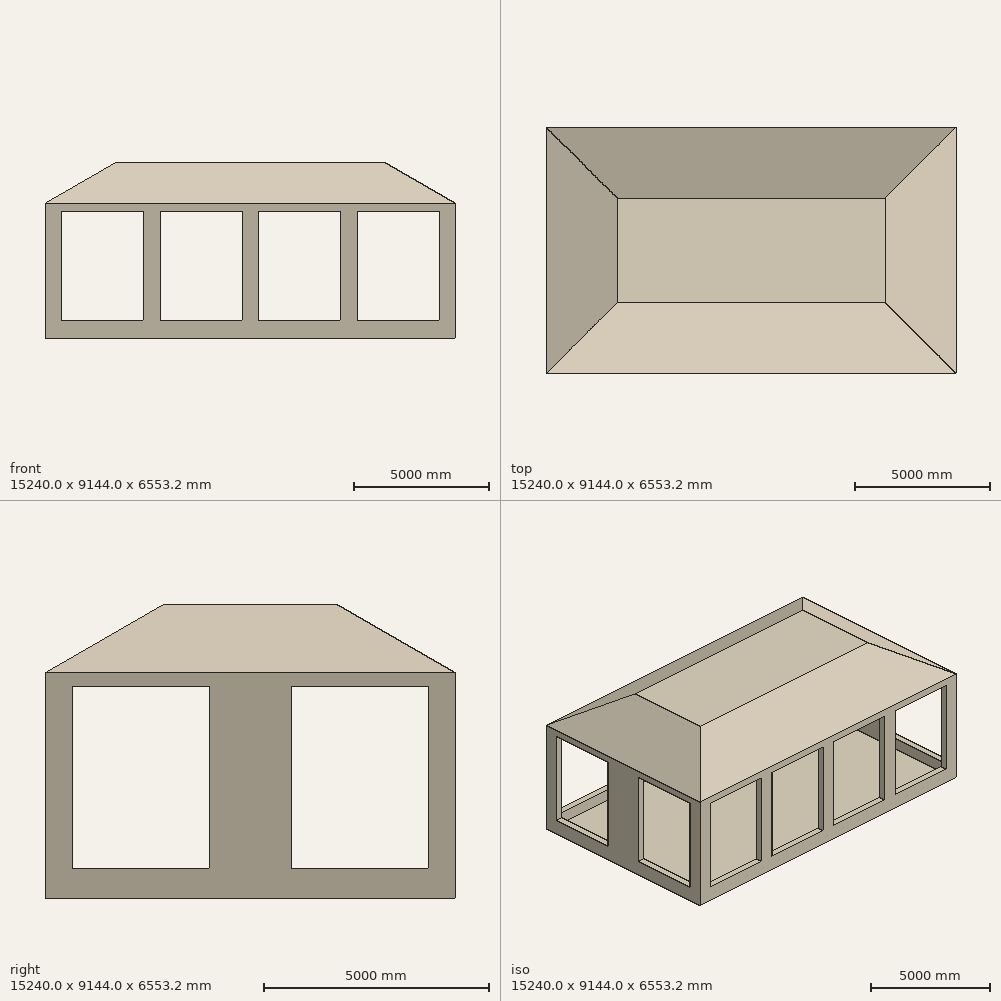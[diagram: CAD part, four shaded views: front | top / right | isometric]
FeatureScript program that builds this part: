
annotation { "Feature Type Name" : "Feature", "Feature Type Description" : "" }
export const myFeature = defineFeature(function(context is Context, id is Id, definition is map)
    precondition{}
    {
        {
            var Q0;
            Q0=qCreatedBy(makeId("Front.planeOp"),FACE);
            var sketch = newSketch(context, id + "F0", { "sketchPlane" : qUnion([Q0])});
            skLineSegment(sketch, "E0.bottom", {"start": v(-2747.34, 3105.4) * mm, "end": v(12492.66, 3105.4) * mm});
            skLineSegment(sketch, "E0.top", {"start": v(-2747.34, -1771.4) * mm, "end": v(12492.66, -1771.4) * mm});
            skLineSegment(sketch, "E0.left", {"start": v(-2747.34, 3105.4) * mm, "end": v(-2747.34, -1771.4) * mm});
            skLineSegment(sketch, "E0.right", {"start": v(12492.66, 3105.4) * mm, "end": v(12492.66, -1771.4) * mm});
            skSolve(sketch);
        }
        {
            var Q0;
            Q0 = qSketchRegion(id + "F0", true);
            extrude(context, id + "F1", {"entities" : qUnion([Q0]), "depth" : 9144 * mm});
        }
        {
            var Q0;
            Q0=makeQuery(id+"F1.opExtrude","SWEPT_FACE",FACE,{"disambiguationData":[OSD([sQuery(id+"F0.wireOp",EDGE,"E0.bottom")])]});
            var sketch = newSketch(context, id + "F2", { "sketchPlane" : qUnion([Q0])});
            skLineSegment(sketch, "E1.bottom", {"start": v(-2747.34, 0) * mm, "end": v(12492.66, 0) * mm});
            skLineSegment(sketch, "E1.top", {"start": v(-2747.34, -9144) * mm, "end": v(12492.66, -9144) * mm});
            skLineSegment(sketch, "E1.left", {"start": v(-2747.34, 0) * mm, "end": v(-2747.34, -9144) * mm});
            skLineSegment(sketch, "E1.right", {"start": v(12492.66, 0) * mm, "end": v(12492.66, -9144) * mm});
            skSolve(sketch);
        }
        {
            var Q0;
            Q0 = qSketchRegion(id + "F2", true);
            extrude(context, id + "F3", {"entities" : qUnion([Q0]), "operationType" : NewBodyOperationType.ADD, "depth" : 1524 * mm, "hasDraft" : true, "draftAngle" : 60 * degree, "draftPullDirection" : true});
        }
        {
            var Q0;
            Q0=makeQuery(id+"F1.opExtrude","SWEPT_FACE",FACE,{"disambiguationData":[OSD([sQuery(id+"F0.wireOp",EDGE,"E0.top")])]});
            shell(context, id + "F4", {"entities" : qUnion([Q0]), "thickness" : 304.8 * mm});
        }
        {
            var Q0;
            Q0=makeQuery(id+"F1.opExtrude","CAP_FACE",FACE,{"disambiguationData":[OSD([sQuery(id+"F0.wireOp",EDGE,"E0.bottom"),sQuery(id+"F0.wireOp",EDGE,"E0.top"),sQuery(id+"F0.wireOp",EDGE,"E0.left"),sQuery(id+"F0.wireOp",EDGE,"E0.right")])],"isStart":false});
            var sketch = newSketch(context, id + "F5", { "sketchPlane" : qUnion([Q0])});
            skLineSegment(sketch, "E2.bottom", {"start": v(-2137.74, 2800.6) * mm, "end": v(910.26, 2800.6) * mm});
            skLineSegment(sketch, "E2.top", {"start": v(-2137.74, -1263.4) * mm, "end": v(910.26, -1263.4) * mm});
            skLineSegment(sketch, "E2.left", {"start": v(-2137.74, 2800.6) * mm, "end": v(-2137.74, -1263.4) * mm});
            skLineSegment(sketch, "E2.right", {"start": v(910.26, 2800.6) * mm, "end": v(910.26, -1263.4) * mm});
            skLineSegment(sketch, "E3.bottom", {"start": v(1519.86, 2800.6) * mm, "end": v(4567.86, 2800.6) * mm});
            skLineSegment(sketch, "E3.top", {"start": v(1519.86, -1263.4) * mm, "end": v(4567.86, -1263.4) * mm});
            skLineSegment(sketch, "E3.left", {"start": v(1519.86, 2800.6) * mm, "end": v(1519.86, -1263.4) * mm});
            skLineSegment(sketch, "E3.right", {"start": v(4567.86, 2800.6) * mm, "end": v(4567.86, -1263.4) * mm});
            skLineSegment(sketch, "E4.bottom", {"start": v(5177.46, 2800.6) * mm, "end": v(8225.46, 2800.6) * mm});
            skLineSegment(sketch, "E4.top", {"start": v(5177.46, -1263.4) * mm, "end": v(8225.46, -1263.4) * mm});
            skLineSegment(sketch, "E4.left", {"start": v(5177.46, 2800.6) * mm, "end": v(5177.46, -1263.4) * mm});
            skLineSegment(sketch, "E4.right", {"start": v(8225.46, 2800.6) * mm, "end": v(8225.46, -1263.4) * mm});
            skLineSegment(sketch, "E5.bottom", {"start": v(8835.06, 2800.6) * mm, "end": v(11883.06, 2800.6) * mm});
            skLineSegment(sketch, "E5.top", {"start": v(8835.06, -1263.4) * mm, "end": v(11883.06, -1263.4) * mm});
            skLineSegment(sketch, "E5.left", {"start": v(8835.06, 2800.6) * mm, "end": v(8835.06, -1263.4) * mm});
            skLineSegment(sketch, "E5.right", {"start": v(11883.06, 2800.6) * mm, "end": v(11883.06, -1263.4) * mm});
            skSolve(sketch);
        }
        {
            var Q0;
            Q0 = qSketchRegion(id + "F5", true);
            extrude(context, id + "F6", {"entities" : qUnion([Q0]), "operationType" : NewBodyOperationType.REMOVE, "endBound" : BoundingType.THROUGH_ALL, "oppositeDirection" : true, "depth" : 25.4 * mm});
        }
        {
            var Q0;
            Q0=makeQuery(id+"F1.opExtrude","SWEPT_FACE",FACE,{"disambiguationData":[OSD([sQuery(id+"F0.wireOp",EDGE,"E0.right")])]});
            var sketch = newSketch(context, id + "F7", { "sketchPlane" : qUnion([Q0])});
            skLineSegment(sketch, "E6.bottom", {"start": v(-8534.4, 2800.6) * mm, "end": v(-5486.4, 2800.6) * mm});
            skLineSegment(sketch, "E6.top", {"start": v(-8534.4, -1263.4) * mm, "end": v(-5486.4, -1263.4) * mm});
            skLineSegment(sketch, "E6.left", {"start": v(-8534.4, 2800.6) * mm, "end": v(-8534.4, -1263.4) * mm});
            skLineSegment(sketch, "E6.right", {"start": v(-5486.4, 2800.6) * mm, "end": v(-5486.4, -1263.4) * mm});
            skLineSegment(sketch, "E7.bottom", {"start": v(-3657.6, 2800.6) * mm, "end": v(-609.6, 2800.6) * mm});
            skLineSegment(sketch, "E7.top", {"start": v(-3657.6, -1263.4) * mm, "end": v(-609.6, -1263.4) * mm});
            skLineSegment(sketch, "E7.left", {"start": v(-3657.6, 2800.6) * mm, "end": v(-3657.6, -1263.4) * mm});
            skLineSegment(sketch, "E7.right", {"start": v(-609.6, 2800.6) * mm, "end": v(-609.6, -1263.4) * mm});
            skSolve(sketch);
        }
        {
            var Q0;
            Q0=makeQuery(id+"F7.imprint","IMPRINT",FACE,{"disambiguationData":[TD([[makeQuery(id+"F7.imprint","IMPRINT",EDGE,{"derivedFrom":sQuery(id+"F7.wireOp",EDGE,"E6.bottom")}),-1.0]])]});
            var Q1;
            Q1=makeQuery(id+"F7.imprint","IMPRINT",FACE,{"disambiguationData":[TD([[makeQuery(id+"F7.imprint","IMPRINT",EDGE,{"derivedFrom":sQuery(id+"F7.wireOp",EDGE,"E7.bottom")}),-1.0]])]});
            extrude(context, id + "F8", {"entities" : qUnion([Q0, Q1]), "operationType" : NewBodyOperationType.REMOVE, "endBound" : BoundingType.THROUGH_ALL, "oppositeDirection" : true, "depth" : 25.4 * mm});
        }
        {
            var Q0;
            Q0=makeQuery(id+"F1.opExtrude","CAP_FACE",FACE,{"disambiguationData":[OSD([sQuery(id+"F0.wireOp",EDGE,"E0.bottom"),sQuery(id+"F0.wireOp",EDGE,"E0.top"),sQuery(id+"F0.wireOp",EDGE,"E0.left"),sQuery(id+"F0.wireOp",EDGE,"E0.right")])],"isStart":false});
            var sketch = newSketch(context, id + "F9", { "sketchPlane" : qUnion([Q0])});
            skLineSegment(sketch, "E8.bottom", {"start": v(-2747.34, -1771.4) * mm, "end": v(12492.66, -1771.4) * mm});
            skLineSegment(sketch, "E8.top", {"start": v(-2747.34, -1923.8) * mm, "end": v(12492.66, -1923.8) * mm});
            skLineSegment(sketch, "E8.left", {"start": v(-2747.34, -1771.4) * mm, "end": v(-2747.34, -1923.8) * mm});
            skLineSegment(sketch, "E8.right", {"start": v(12492.66, -1771.4) * mm, "end": v(12492.66, -1923.8) * mm});
            skSolve(sketch);
        }
        {
            var Q0;
            Q0 = qSketchRegion(id + "F9", true);
            extrude(context, id + "F10", {"entities" : qUnion([Q0]), "operationType" : NewBodyOperationType.ADD, "oppositeDirection" : true, "depth" : 9144 * mm});
        }
    });
